# Revit family: HVAC_Mechanical-Ventilation_Envira-North_Alite-3_Ceiling-Fan2
name_source: partatom
category: Electrical Fixtures
units: mm (PartAtom-declared; Revit-internal decimal feet)

## family parameters
Always vertical = No
Cut with Voids When Loaded = No
Maintain Annotation Orientation = No
OmniClass Number = 23.75.35.17.17.11
OmniClass Title = Ceiling Fans
Part Type = Normal
Room Calculation Point = No
Round Connector Dimension = Use Diameter
Shared = No
Work Plane-Based = Yes

## types (2) — shared parameters
Alternate Voltage = 460 V
CFEI 40% Speed = 1 ft³·h/(min·Btu)
Date Updated = 17/12/2024
Default Elevation = 0.00"
Description = Alite 3 HVLS Fan
Manufacturer = Envira-North Systems
Number of Poles = 3
Power Factor = 1
Product Material = Envira North Systems - Metal
Product Page URL = https://www.enviranorth.com
Sound Rating = 62
URL = https://www.enviranorth.com
Version = 1
Voltage = 230 V
Wattage = 368 W
z_Clearence Blades = 30.00"
z_Clearence to Floor = 144.00"
z_Extension Type 2FT = Extension Mount : 2FT
z_Extension Type 4FT = Extension Mount : 4FT
z_Standard Mount 1FT = Mount Length : 1FT
z_Standard Mount 2FT = Mount Length : 2FT
z_Standard Mount 4FT = Mount Length : 4FT
zero-valued in all types: CFEI High Speed

## per-type parameters (varying)
| type | Design Ventilation Air Flow | Diameter | Maximum Effective Diameter | Maximum Velocity | Model | Weight | z_Blades Length 2 | z_Clearence Blades Diameter | z_Radius |
| EN780X0166 - 15FT | 52662 CFM | 180.00" | 720.00" | 389 FPM | EN780X0066 | 168.00 lbf | Blade : 15FT | 216.00" | 90.00" |
| EN780X0174 - 23FT | 177184 CFM | 276.00" | 2760.00" | 439 FPM | EN780X0074 | 347.00 lbf | Blade : 23FT | 312.00" | 138.00" |

## geometry (parser evidence)
native form markers: Sweep x9
no freeform markers — native parametric forms only
